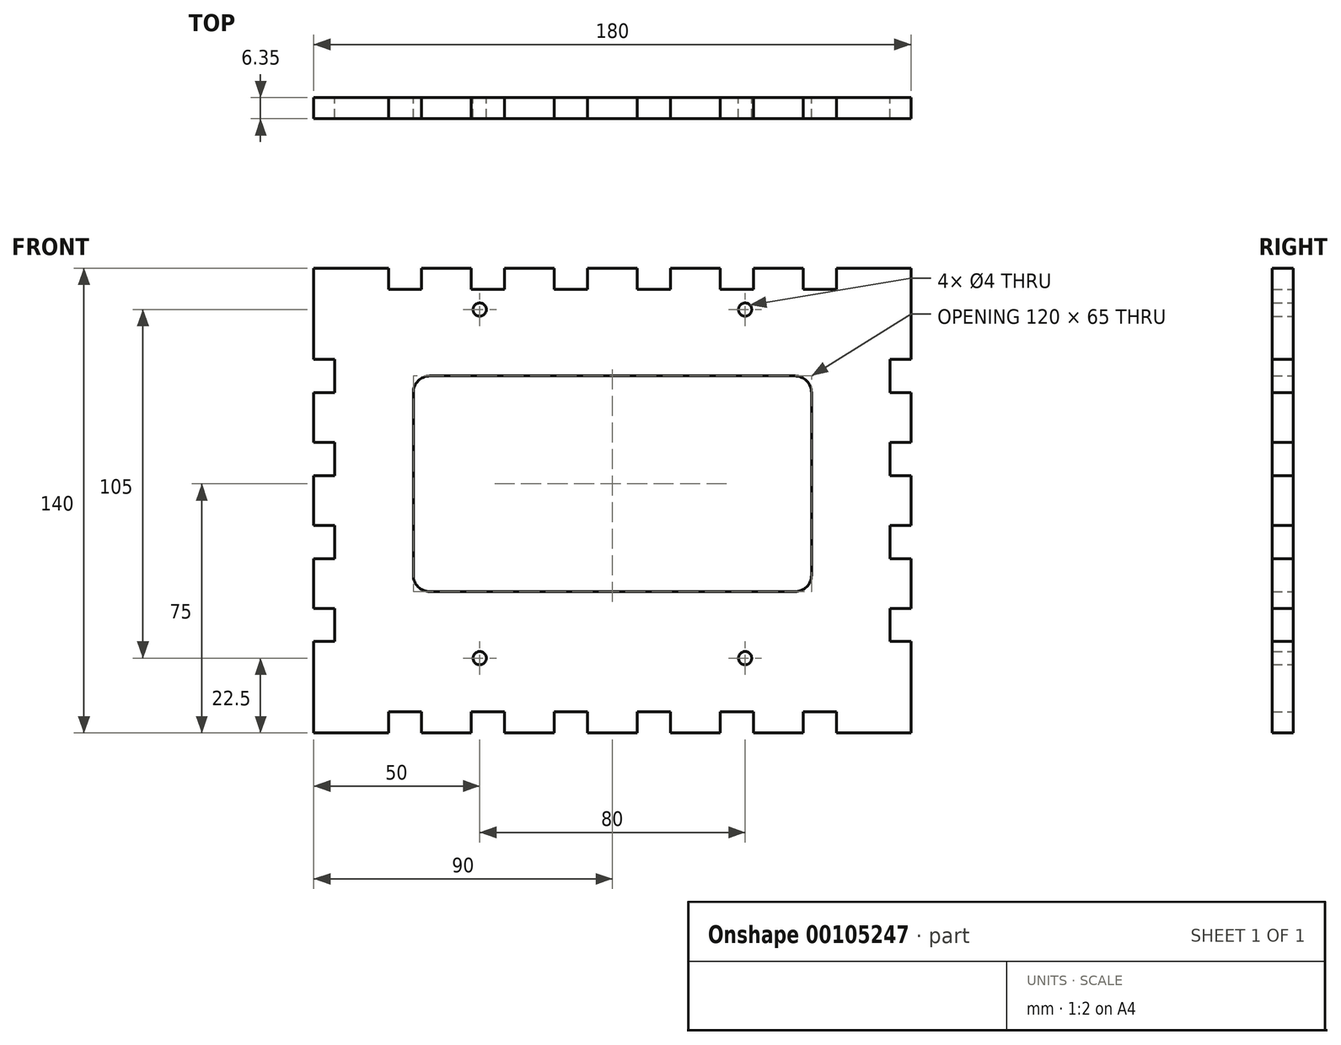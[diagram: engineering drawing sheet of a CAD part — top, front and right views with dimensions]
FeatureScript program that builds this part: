
annotation { "Feature Type Name" : "Feature", "Feature Type Description" : "" }
export const myFeature = defineFeature(function(context is Context, id is Id, definition is map)
    precondition{}
    {
        {
            var Q0;
            Q0=qCreatedBy(makeId("Front.planeOp"),FACE);
            var sketch = newSketch(context, id + "F0", { "sketchPlane" : qUnion([Q0])});
            skLineSegment(sketch, "E0.bottom", {"start": v(180, 140) * mm, "end": v(157.5, 140) * mm});
            skLineSegment(sketch, "E0.top", {"start": v(180, 0) * mm, "end": v(157.5, 0) * mm});
            skLineSegment(sketch, "E0.left", {"start": v(180, 140) * mm, "end": v(180, 112.5) * mm});
            skLineSegment(sketch, "E0.right", {"start": v(0, 140) * mm, "end": v(0, 112.5) * mm});
            skLineSegment(sketch, "E1.top", {"start": v(22.5, 133.65) * mm, "end": v(32.5, 133.65) * mm});
            skLineSegment(sketch, "E1.left", {"start": v(22.5, 140) * mm, "end": v(22.5, 133.65) * mm});
            skLineSegment(sketch, "E1.right", {"start": v(32.5, 140) * mm, "end": v(32.5, 133.65) * mm});
            skLineSegment(sketch, "E2.trimOffspring", {"start": v(22.5, 140) * mm, "end": v(0, 140) * mm});
            skLineSegment(sketch, "E3.1.0.0", {"start": v(47.5, 133.65) * mm, "end": v(57.5, 133.65) * mm});
            skLineSegment(sketch, "E3.1.0.1", {"start": v(57.5, 140) * mm, "end": v(57.5, 133.65) * mm});
            skLineSegment(sketch, "E3.1.0.2", {"start": v(47.5, 140) * mm, "end": v(47.5, 133.65) * mm});
            skLineSegment(sketch, "E3.2.0.0", {"start": v(72.5, 133.65) * mm, "end": v(82.5, 133.65) * mm});
            skLineSegment(sketch, "E3.2.0.1", {"start": v(82.5, 140) * mm, "end": v(82.5, 133.65) * mm});
            skLineSegment(sketch, "E3.2.0.2", {"start": v(72.5, 140) * mm, "end": v(72.5, 133.65) * mm});
            skLineSegment(sketch, "E3.3.0.0", {"start": v(97.5, 133.65) * mm, "end": v(107.5, 133.65) * mm});
            skLineSegment(sketch, "E3.3.0.1", {"start": v(107.5, 140) * mm, "end": v(107.5, 133.65) * mm});
            skLineSegment(sketch, "E3.3.0.2", {"start": v(97.5, 140) * mm, "end": v(97.5, 133.65) * mm});
            skLineSegment(sketch, "E3.4.0.0", {"start": v(122.5, 133.65) * mm, "end": v(132.5, 133.65) * mm});
            skLineSegment(sketch, "E3.4.0.1", {"start": v(132.5, 140) * mm, "end": v(132.5, 133.65) * mm});
            skLineSegment(sketch, "E3.4.0.2", {"start": v(122.5, 140) * mm, "end": v(122.5, 133.65) * mm});
            skLineSegment(sketch, "E3.5.0.0", {"start": v(147.5, 133.65) * mm, "end": v(157.5, 133.65) * mm});
            skLineSegment(sketch, "E3.5.0.1", {"start": v(157.5, 140) * mm, "end": v(157.5, 133.65) * mm});
            skLineSegment(sketch, "E3.5.0.2", {"start": v(147.5, 140) * mm, "end": v(147.5, 133.65) * mm});
            skLineSegment(sketch, "E3.direction1", {"start": v(22.5, 133.65) * mm, "end": v(47.5, 133.65) * mm, "construction": true});
            skLineSegment(sketch, "E4.trimOffspring", {"start": v(47.5, 140) * mm, "end": v(32.5, 140) * mm});
            skLineSegment(sketch, "E5.trimOffspring", {"start": v(72.5, 140) * mm, "end": v(57.5, 140) * mm});
            skLineSegment(sketch, "E6.trimOffspring", {"start": v(97.5, 140) * mm, "end": v(82.5, 140) * mm});
            skLineSegment(sketch, "E7.trimOffspring", {"start": v(122.5, 140) * mm, "end": v(107.5, 140) * mm});
            skLineSegment(sketch, "E8.trimOffspring", {"start": v(147.5, 140) * mm, "end": v(132.5, 140) * mm});
            skLineSegment(sketch, "E9", {"start": v(0, 70) * mm, "end": v(180, 70) * mm, "construction": true});
            skLineSegment(sketch, "E10.MirrorCS", {"start": v(22.5, 6.35) * mm, "end": v(32.5, 6.35) * mm});
            skLineSegment(sketch, "E11.MirrorCS", {"start": v(157.5, 0) * mm, "end": v(157.5, 6.35) * mm});
            skLineSegment(sketch, "E12.MirrorCS", {"start": v(122.5, 6.35) * mm, "end": v(132.5, 6.35) * mm});
            skLineSegment(sketch, "E13.MirrorCS", {"start": v(97.5, 0) * mm, "end": v(82.5, 0) * mm});
            skLineSegment(sketch, "E14.MirrorCS", {"start": v(122.5, 0) * mm, "end": v(122.5, 6.35) * mm});
            skLineSegment(sketch, "E15.MirrorCS", {"start": v(72.5, 0) * mm, "end": v(72.5, 6.35) * mm});
            skLineSegment(sketch, "E16.MirrorCS", {"start": v(97.5, 6.35) * mm, "end": v(107.5, 6.35) * mm});
            skLineSegment(sketch, "E17.MirrorCS", {"start": v(107.5, 0) * mm, "end": v(107.5, 6.35) * mm});
            skLineSegment(sketch, "E18.MirrorCS", {"start": v(72.5, 0) * mm, "end": v(57.5, 0) * mm});
            skLineSegment(sketch, "E19.MirrorCS", {"start": v(147.5, 0) * mm, "end": v(147.5, 6.35) * mm});
            skLineSegment(sketch, "E20.MirrorCS", {"start": v(132.5, 0) * mm, "end": v(132.5, 6.35) * mm});
            skLineSegment(sketch, "E21.MirrorCS", {"start": v(22.5, 0) * mm, "end": v(22.5, 6.35) * mm});
            skLineSegment(sketch, "E22.MirrorCS", {"start": v(32.5, 0) * mm, "end": v(32.5, 6.35) * mm});
            skLineSegment(sketch, "E23.MirrorCS", {"start": v(72.5, 6.35) * mm, "end": v(82.5, 6.35) * mm});
            skLineSegment(sketch, "E24.MirrorCS", {"start": v(57.5, 0) * mm, "end": v(57.5, 6.35) * mm});
            skLineSegment(sketch, "E25.MirrorCS", {"start": v(82.5, 0) * mm, "end": v(82.5, 6.35) * mm});
            skLineSegment(sketch, "E26.MirrorCS", {"start": v(122.5, 0) * mm, "end": v(107.5, 0) * mm});
            skLineSegment(sketch, "E27.MirrorCS", {"start": v(22.5, 6.35) * mm, "end": v(47.5, 6.35) * mm, "construction": true});
            skLineSegment(sketch, "E28.MirrorCS", {"start": v(147.5, 6.35) * mm, "end": v(157.5, 6.35) * mm});
            skLineSegment(sketch, "E29.MirrorCS", {"start": v(147.5, 0) * mm, "end": v(132.5, 0) * mm});
            skLineSegment(sketch, "E30.MirrorCS", {"start": v(47.5, 6.35) * mm, "end": v(57.5, 6.35) * mm});
            skLineSegment(sketch, "E31.MirrorCS", {"start": v(47.5, 0) * mm, "end": v(32.5, 0) * mm});
            skLineSegment(sketch, "E32.MirrorCS", {"start": v(47.5, 0) * mm, "end": v(47.5, 6.35) * mm});
            skLineSegment(sketch, "E33.MirrorCS", {"start": v(97.5, 0) * mm, "end": v(97.5, 6.35) * mm});
            skLineSegment(sketch, "E34.trimOffspring", {"start": v(22.5, 0) * mm, "end": v(0, 0) * mm});
            skLineSegment(sketch, "E35.bottom", {"start": v(180, 112.5) * mm, "end": v(173.65, 112.5) * mm});
            skLineSegment(sketch, "E35.top", {"start": v(180, 102.5) * mm, "end": v(173.65, 102.5) * mm});
            skLineSegment(sketch, "E35.right", {"start": v(173.65, 112.5) * mm, "end": v(173.65, 102.5) * mm});
            skLineSegment(sketch, "E36.0.1.1", {"start": v(180, 87.5) * mm, "end": v(173.65, 87.5) * mm});
            skLineSegment(sketch, "E36.0.1.2", {"start": v(173.65, 87.5) * mm, "end": v(173.65, 77.5) * mm});
            skLineSegment(sketch, "E36.0.1.3", {"start": v(180, 77.5) * mm, "end": v(173.65, 77.5) * mm});
            skLineSegment(sketch, "E36.0.2.1", {"start": v(180, 62.5) * mm, "end": v(173.65, 62.5) * mm});
            skLineSegment(sketch, "E36.0.2.2", {"start": v(173.65, 62.5) * mm, "end": v(173.65, 52.5) * mm});
            skLineSegment(sketch, "E36.0.2.3", {"start": v(180, 52.5) * mm, "end": v(173.65, 52.5) * mm});
            skLineSegment(sketch, "E36.0.3.1", {"start": v(180, 37.5) * mm, "end": v(173.65, 37.5) * mm});
            skLineSegment(sketch, "E36.0.3.2", {"start": v(173.65, 37.5) * mm, "end": v(173.65, 27.5) * mm});
            skLineSegment(sketch, "E36.0.3.3", {"start": v(180, 27.5) * mm, "end": v(173.65, 27.5) * mm});
            skLineSegment(sketch, "E36.direction1", {"start": v(173.65, 102.5) * mm, "end": v(195, 102.5) * mm, "construction": true});
            skLineSegment(sketch, "E36.direction2", {"start": v(173.65, 102.5) * mm, "end": v(173.65, 77.5) * mm, "construction": true});
            skLineSegment(sketch, "E37.trimOffspring", {"start": v(180, 102.5) * mm, "end": v(180, 87.5) * mm});
            skLineSegment(sketch, "E38.trimOffspring", {"start": v(180, 52.5) * mm, "end": v(180, 37.5) * mm});
            skLineSegment(sketch, "E39.trimOffspring", {"start": v(180, 77.5) * mm, "end": v(180, 62.5) * mm});
            skLineSegment(sketch, "E40.trimOffspring", {"start": v(180, 27.5) * mm, "end": v(180, 0) * mm});
            skLineSegment(sketch, "E41", {"start": v(90, 140) * mm, "end": v(90, 0) * mm, "construction": true});
            skLineSegment(sketch, "E42.MirrorCS", {"start": v(0, 52.5) * mm, "end": v(6.35, 52.5) * mm});
            skLineSegment(sketch, "E43.MirrorCS", {"start": v(0, 102.5) * mm, "end": v(6.35, 102.5) * mm});
            skLineSegment(sketch, "E44.MirrorCS", {"start": v(0, 27.5) * mm, "end": v(6.35, 27.5) * mm});
            skLineSegment(sketch, "E45.MirrorCS", {"start": v(0, 112.5) * mm, "end": v(6.35, 112.5) * mm});
            skLineSegment(sketch, "E46.MirrorCS", {"start": v(0, 37.5) * mm, "end": v(6.35, 37.5) * mm});
            skLineSegment(sketch, "E47.MirrorCS", {"start": v(0, 77.5) * mm, "end": v(6.35, 77.5) * mm});
            skLineSegment(sketch, "E48.MirrorCS", {"start": v(0, 87.5) * mm, "end": v(6.35, 87.5) * mm});
            skLineSegment(sketch, "E49.MirrorCS", {"start": v(0, 62.5) * mm, "end": v(6.35, 62.5) * mm});
            skLineSegment(sketch, "E50.MirrorCS", {"start": v(6.35, 87.5) * mm, "end": v(6.35, 77.5) * mm});
            skLineSegment(sketch, "E51.MirrorCS", {"start": v(0, 77.5) * mm, "end": v(0, 62.5) * mm});
            skLineSegment(sketch, "E52.MirrorCS", {"start": v(6.35, 37.5) * mm, "end": v(6.35, 27.5) * mm});
            skLineSegment(sketch, "E53.MirrorCS", {"start": v(0, 52.5) * mm, "end": v(0, 37.5) * mm});
            skLineSegment(sketch, "E54.MirrorCS", {"start": v(6.35, 62.5) * mm, "end": v(6.35, 52.5) * mm});
            skLineSegment(sketch, "E55.MirrorCS", {"start": v(6.35, 112.5) * mm, "end": v(6.35, 102.5) * mm});
            skLineSegment(sketch, "E56.MirrorCS", {"start": v(0, 102.5) * mm, "end": v(0, 87.5) * mm});
            skLineSegment(sketch, "E57.MirrorCS", {"start": v(6.35, 102.5) * mm, "end": v(6.35, 77.5) * mm, "construction": true});
            skLineSegment(sketch, "E58.trimOffspring", {"start": v(0, 27.5) * mm, "end": v(0, 0) * mm});
            skPoint(sketch, "E59", {"position": v(130, 127.5) * mm});
            skPoint(sketch, "E60", {"position": v(130, 22.5) * mm});
            skPoint(sketch, "E61", {"position": v(50, 127.5) * mm});
            skPoint(sketch, "E62", {"position": v(50, 22.5) * mm});
            skLineSegment(sketch, "E63.bottom", {"start": v(35, 107.5) * mm, "end": v(145, 107.5) * mm});
            skLineSegment(sketch, "E63.top", {"start": v(35, 42.5) * mm, "end": v(145, 42.5) * mm});
            skLineSegment(sketch, "E63.left", {"start": v(30, 102.5) * mm, "end": v(30, 47.5) * mm});
            skLineSegment(sketch, "E63.right", {"start": v(150, 102.5) * mm, "end": v(150, 47.5) * mm});
            skPoint(sketch, "E64.visualSharp", {"position": v(30, 107.5) * mm});
            skArc(sketch, "E64.filletArc", {"start": v(35, 107.5) * mm, "mid": v(31.46, 106.04) * mm, "end": v(30, 102.5) * mm});
            skPoint(sketch, "E65.visualSharp", {"position": v(30, 42.5) * mm});
            skArc(sketch, "E65.filletArc", {"start": v(30, 47.5) * mm, "mid": v(31.46, 43.96) * mm, "end": v(35, 42.5) * mm});
            skPoint(sketch, "E66.visualSharp", {"position": v(150, 42.5) * mm});
            skArc(sketch, "E66.filletArc", {"start": v(145, 42.5) * mm, "mid": v(148.54, 43.96) * mm, "end": v(150, 47.5) * mm});
            skPoint(sketch, "E67.visualSharp", {"position": v(150, 107.5) * mm});
            skArc(sketch, "E67.filletArc", {"start": v(150, 102.5) * mm, "mid": v(148.54, 106.04) * mm, "end": v(145, 107.5) * mm});
            skCircle(sketch, "E68", {"center": v(50, 127.5) * mm, "radius": 1.5 * mm});
            skCircle(sketch, "E69.MirrorC", {"center": v(130, 127.5) * mm, "radius": 1.5 * mm});
            skCircle(sketch, "E70", {"center": v(50, 22.5) * mm, "radius": 1.5 * mm});
            skCircle(sketch, "E71", {"center": v(130, 22.5) * mm, "radius": 1.5 * mm});
            skSolve(sketch);
        }
        {
            var Q0;
            Q0=makeQuery(id+"F0.imprint","IMPRINT",FACE,{"disambiguationData":[TD([[makeQuery(id+"F0.imprint","IMPRINT",EDGE,{"derivedFrom":sQuery(id+"F0.wireOp",EDGE,"E0.bottom")}),1.0]])]});
            extrude(context, id + "F1", {"entities" : qUnion([Q0]), "depth" : 6.35 * mm});
        }
        {
            var Q0;
            Q0=sQuery(id+"F0.wireOp",VERTEX,"E61");
            var Q1;
            Q1=sQuery(id+"F0.wireOp",VERTEX,"E59");
            var Q2;
            Q2=sQuery(id+"F0.wireOp",VERTEX,"E60");
            var Q3;
            Q3=sQuery(id+"F0.wireOp",VERTEX,"E62");
            var Q4;
            Q4=makeQuery(id+"F1.opExtrude","SWEPT_BODY",BODY,{"disambiguationData":[OSD([sQuery(id+"F0.wireOp",EDGE,"E0.bottom"),sQuery(id+"F0.wireOp",EDGE,"E0.top"),sQuery(id+"F0.wireOp",EDGE,"E0.left"),sQuery(id+"F0.wireOp",EDGE,"E0.right"),sQuery(id+"F0.wireOp",EDGE,"E1.top"),sQuery(id+"F0.wireOp",EDGE,"E1.left"),sQuery(id+"F0.wireOp",EDGE,"E1.right"),sQuery(id+"F0.wireOp",EDGE,"E2.trimOffspring"),sQuery(id+"F0.wireOp",EDGE,"E3.1.0.0"),sQuery(id+"F0.wireOp",EDGE,"E3.1.0.1"),sQuery(id+"F0.wireOp",EDGE,"E3.1.0.2"),sQuery(id+"F0.wireOp",EDGE,"E3.2.0.0"),sQuery(id+"F0.wireOp",EDGE,"E3.2.0.1"),sQuery(id+"F0.wireOp",EDGE,"E3.2.0.2"),sQuery(id+"F0.wireOp",EDGE,"E3.3.0.0"),sQuery(id+"F0.wireOp",EDGE,"E3.3.0.1"),sQuery(id+"F0.wireOp",EDGE,"E3.3.0.2"),sQuery(id+"F0.wireOp",EDGE,"E3.4.0.0"),sQuery(id+"F0.wireOp",EDGE,"E3.4.0.1"),sQuery(id+"F0.wireOp",EDGE,"E3.4.0.2"),sQuery(id+"F0.wireOp",EDGE,"E3.5.0.0"),sQuery(id+"F0.wireOp",EDGE,"E3.5.0.1"),sQuery(id+"F0.wireOp",EDGE,"E3.5.0.2"),sQuery(id+"F0.wireOp",EDGE,"E4.trimOffspring"),sQuery(id+"F0.wireOp",EDGE,"E5.trimOffspring"),sQuery(id+"F0.wireOp",EDGE,"E6.trimOffspring"),sQuery(id+"F0.wireOp",EDGE,"E7.trimOffspring"),sQuery(id+"F0.wireOp",EDGE,"E8.trimOffspring"),sQuery(id+"F0.wireOp",EDGE,"E10.MirrorCS"),sQuery(id+"F0.wireOp",EDGE,"E11.MirrorCS"),sQuery(id+"F0.wireOp",EDGE,"E12.MirrorCS"),sQuery(id+"F0.wireOp",EDGE,"E14.MirrorCS"),sQuery(id+"F0.wireOp",EDGE,"E15.MirrorCS"),sQuery(id+"F0.wireOp",EDGE,"E16.MirrorCS"),sQuery(id+"F0.wireOp",EDGE,"E17.MirrorCS"),sQuery(id+"F0.wireOp",EDGE,"E19.MirrorCS"),sQuery(id+"F0.wireOp",EDGE,"E20.MirrorCS"),sQuery(id+"F0.wireOp",EDGE,"E21.MirrorCS"),sQuery(id+"F0.wireOp",EDGE,"E22.MirrorCS"),sQuery(id+"F0.wireOp",EDGE,"E23.MirrorCS"),sQuery(id+"F0.wireOp",EDGE,"E24.MirrorCS"),sQuery(id+"F0.wireOp",EDGE,"E25.MirrorCS"),sQuery(id+"F0.wireOp",EDGE,"E28.MirrorCS"),sQuery(id+"F0.wireOp",EDGE,"E30.MirrorCS"),sQuery(id+"F0.wireOp",EDGE,"E32.MirrorCS"),sQuery(id+"F0.wireOp",EDGE,"E33.MirrorCS"),sQuery(id+"F0.wireOp",EDGE,"E34.trimOffspring"),sQuery(id+"F0.wireOp",EDGE,"E31.MirrorCS"),sQuery(id+"F0.wireOp",EDGE,"E18.MirrorCS"),sQuery(id+"F0.wireOp",EDGE,"E13.MirrorCS"),sQuery(id+"F0.wireOp",EDGE,"E26.MirrorCS"),sQuery(id+"F0.wireOp",EDGE,"E29.MirrorCS"),sQuery(id+"F0.wireOp",EDGE,"E35.bottom"),sQuery(id+"F0.wireOp",EDGE,"E35.top"),sQuery(id+"F0.wireOp",EDGE,"E35.right"),sQuery(id+"F0.wireOp",EDGE,"E36.0.1.1"),sQuery(id+"F0.wireOp",EDGE,"E36.0.1.2"),sQuery(id+"F0.wireOp",EDGE,"E36.0.1.3"),sQuery(id+"F0.wireOp",EDGE,"E36.0.2.1"),sQuery(id+"F0.wireOp",EDGE,"E36.0.2.2"),sQuery(id+"F0.wireOp",EDGE,"E36.0.2.3"),sQuery(id+"F0.wireOp",EDGE,"E36.0.3.1"),sQuery(id+"F0.wireOp",EDGE,"E36.0.3.2"),sQuery(id+"F0.wireOp",EDGE,"E36.0.3.3"),sQuery(id+"F0.wireOp",EDGE,"E37.trimOffspring"),sQuery(id+"F0.wireOp",EDGE,"E38.trimOffspring"),sQuery(id+"F0.wireOp",EDGE,"E39.trimOffspring"),sQuery(id+"F0.wireOp",EDGE,"E40.trimOffspring"),sQuery(id+"F0.wireOp",EDGE,"E42.MirrorCS"),sQuery(id+"F0.wireOp",EDGE,"E43.MirrorCS"),sQuery(id+"F0.wireOp",EDGE,"E44.MirrorCS"),sQuery(id+"F0.wireOp",EDGE,"E45.MirrorCS"),sQuery(id+"F0.wireOp",EDGE,"E46.MirrorCS"),sQuery(id+"F0.wireOp",EDGE,"E47.MirrorCS"),sQuery(id+"F0.wireOp",EDGE,"E48.MirrorCS"),sQuery(id+"F0.wireOp",EDGE,"E49.MirrorCS"),sQuery(id+"F0.wireOp",EDGE,"E50.MirrorCS"),sQuery(id+"F0.wireOp",EDGE,"E52.MirrorCS"),sQuery(id+"F0.wireOp",EDGE,"E54.MirrorCS"),sQuery(id+"F0.wireOp",EDGE,"E55.MirrorCS"),sQuery(id+"F0.wireOp",EDGE,"E56.MirrorCS"),sQuery(id+"F0.wireOp",EDGE,"E51.MirrorCS"),sQuery(id+"F0.wireOp",EDGE,"E53.MirrorCS"),sQuery(id+"F0.wireOp",EDGE,"E58.trimOffspring")])]});
            hole(context, id + "F2", {"style" : HoleStyle.SIMPLE, "endStyle" : HoleEndStyle.THROUGH, "oppositeDirection" : true, "holeDiameter" : 4 * mm, "locations" : qUnion([Q0, Q1, Q2, Q3]), "scope" : qUnion([Q4]), "isTappedThrough" : true});
        }
    });
